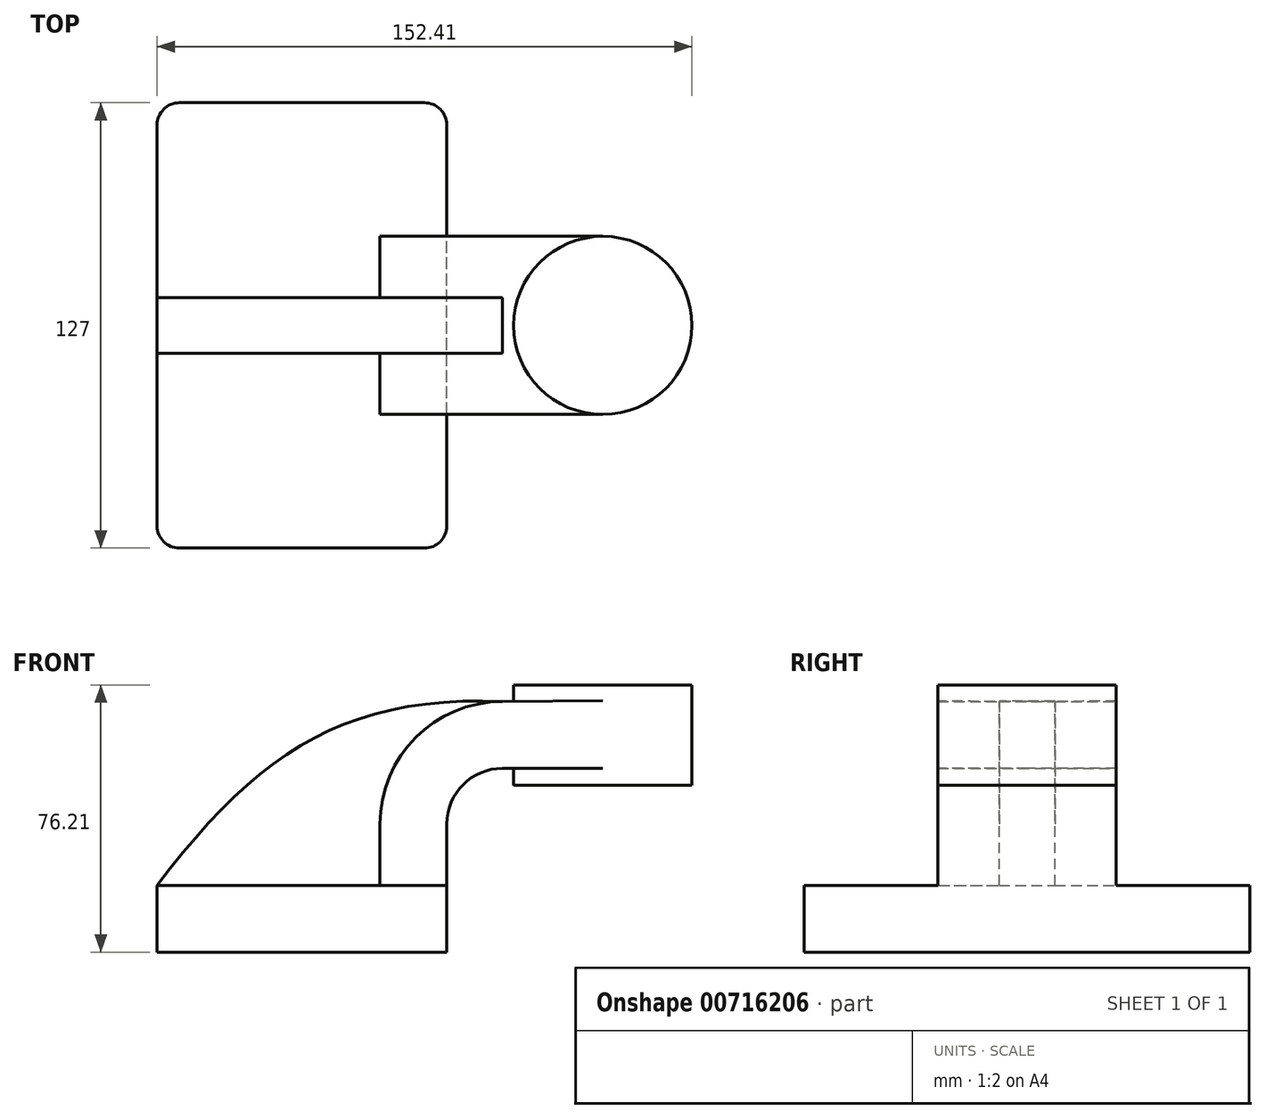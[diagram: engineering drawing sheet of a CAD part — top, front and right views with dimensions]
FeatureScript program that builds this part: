
annotation { "Feature Type Name" : "Feature", "Feature Type Description" : "" }
export const myFeature = defineFeature(function(context is Context, id is Id, definition is map)
    precondition{}
    {
        {
            var Q0;
            Q0=qCreatedBy(makeId("Front.planeOp"),FACE);
            var sketch = newSketch(context, id + "F0", { "sketchPlane" : qUnion([Q0])});
            skLineSegment(sketch, "E0.bottom", {"start": v(-41.28, 9.52) * mm, "end": v(41.28, 9.53) * mm});
            skLineSegment(sketch, "E0.top", {"start": v(-41.27, -9.53) * mm, "end": v(41.28, -9.53) * mm});
            skLineSegment(sketch, "E0.left", {"start": v(-41.28, 9.53) * mm, "end": v(-41.28, -9.53) * mm});
            skLineSegment(sketch, "E0.right", {"start": v(41.27, 9.53) * mm, "end": v(41.28, -9.52) * mm});
            skPoint(sketch, "E0.middle", {"position": v(0, 0) * mm});
            skLineSegment(sketch, "E1.bottom", {"start": v(60.32, 38.1) * mm, "end": v(111.12, 38.1) * mm});
            skLineSegment(sketch, "E1.top", {"start": v(60.32, 66.67) * mm, "end": v(111.12, 66.67) * mm});
            skLineSegment(sketch, "E1.left", {"start": v(60.32, 38.1) * mm, "end": v(60.32, 66.67) * mm});
            skLineSegment(sketch, "E1.right", {"start": v(111.12, 38.1) * mm, "end": v(111.12, 66.67) * mm});
            skPoint(sketch, "E1.middle", {"position": v(85.72, 52.39) * mm});
            skLineSegment(sketch, "E2", {"start": v(41.27, 9.53) * mm, "end": v(41.27, 27) * mm});
            skArc(sketch, "E3", {"start": v(41.27, 27) * mm, "mid": v(45.92, 38.23) * mm, "end": v(57.15, 42.88) * mm});
            skLineSegment(sketch, "E4", {"start": v(57.15, 42.88) * mm, "end": v(113.46, 42.88) * mm});
            skLineSegment(sketch, "E5.2", {"start": v(168.27, 9.53) * mm, "end": v(168.27, 27) * mm});
            skLineSegment(sketch, "E6.0", {"start": v(22.22, 9.53) * mm, "end": v(22.22, 27) * mm});
            skArc(sketch, "E7.0", {"start": v(22.22, 27) * mm, "mid": v(32.45, 51.7) * mm, "end": v(57.15, 61.93) * mm});
            skLineSegment(sketch, "E8", {"start": v(57.15, 61.93) * mm, "end": v(85.72, 62.13) * mm});
            skLineSegment(sketch, "E9", {"start": v(85.72, 38.1) * mm, "end": v(85.72, 66.67) * mm});
            skFitSpline(sketch, "E10", {"points": [v(-41.28, 9.52) * mm, v(57.15, 61.93) * mm], "startDerivative": vector(85.03, 112.26) * mm, "endDerivative": vector(136.02, -5.67) * mm});
            skSolve(sketch);
        }
        {
            var Q0;
            Q0=makeQuery(id+"F0.imprint","IMPRINT",FACE,{"disambiguationData":[TD([[makeQuery(id+"F0.imprint","IMPRINT",EDGE,{"derivedFrom":sQuery(id+"F0.wireOp",EDGE,"E0.top")}),1.0]])]});
            extrude(context, id + "F1", {"entities" : qUnion([Q0]), "endBound" : BoundingType.SYMMETRIC, "depth" : 127 * mm, "offsetDistance" : 25.4 * mm});
        }
        {
            var Q0;
            {var subQ0=sQuery(id+"F0.wireOp",EDGE,"E2");Q0=makeQuery(id+"F0.imprint","IMPRINT",FACE,{"disambiguationData":[TD([[makeQuery(id+"F0.imprint","IMPRINT",EDGE,{"derivedFrom":subQ0}),1.0]])]});}
            var Q1;
            {var subQ0=sQuery(id+"F0.wireOp",EDGE,"E4");var subQ1=sQuery(id+"F0.wireOp",EDGE,"E1.left");var subQ2=makeQuery(id+"F0.imprint","INTERSECT",VERTEX,{"derivedFrom":[subQ1,subQ0]});Q1=makeQuery(id+"F0.imprint","IMPRINT",FACE,{"disambiguationData":[TD([[makeQuery(id+"F0.imprint","IMPRINT",EDGE,{"disambiguationData":[TD([[subQ2,-1.0]])],"derivedFrom":subQ1}),-1.0]])]});}
            extrude(context, id + "F2", {"entities" : qUnion([Q0, Q1]), "operationType" : NewBodyOperationType.ADD, "endBound" : BoundingType.SYMMETRIC, "depth" : 50.8 * mm, "offsetDistance" : 25.4 * mm});
        }
        {
            var Q0;
            {var subQ2=sQuery(id+"F0.wireOp",EDGE,"E6.0");Q0=makeQuery(id+"F0.imprint","IMPRINT",FACE,{"disambiguationData":[TD([[makeQuery(id+"F0.imprint","IMPRINT",EDGE,{"derivedFrom":subQ2}),1.0]])]});}
            extrude(context, id + "F3", {"entities" : qUnion([Q0]), "operationType" : NewBodyOperationType.ADD, "endBound" : BoundingType.SYMMETRIC, "depth" : 15.88 * mm, "offsetDistance" : 25.4 * mm});
        }
        {
            var Q0;
            {var subQ4=sQuery(id+"F0.wireOp",EDGE,"E1.right");var subQ5=sQuery(id+"F0.wireOp",EDGE,"E1.top");var subQ6=makeQuery(id+"F0.imprint","INTERSECT",VERTEX,{"derivedFrom":[subQ5,subQ4]});Q0=makeQuery(id+"F0.imprint","IMPRINT",FACE,{"disambiguationData":[TD([[makeQuery(id+"F0.imprint","IMPRINT",EDGE,{"disambiguationData":[TD([[subQ6,1.0]])],"derivedFrom":subQ5}),-1.0]])]});}
            var Q1;
            {var subQ0=sQuery(id+"F0.wireOp",EDGE,"E1.right");var subQ1=sQuery(id+"F0.wireOp",EDGE,"E1.bottom");var subQ2=makeQuery(id+"F0.imprint","INTERSECT",VERTEX,{"derivedFrom":[subQ1,subQ0]});Q1=makeQuery(id+"F0.imprint","IMPRINT",FACE,{"disambiguationData":[TD([[makeQuery(id+"F0.imprint","IMPRINT",EDGE,{"disambiguationData":[TD([[subQ2,1.0]])],"derivedFrom":subQ1}),1.0]])]});}
            var Q2;
            Q2=sQuery(id+"F0.wireOp",EDGE,"E9");
            revolve(context, id + "F4", {"operationType" : NewBodyOperationType.ADD, "surfaceOperationType" : NewSurfaceOperationType.NEW, "entities" : qUnion([Q0, Q1]), "axis" : qUnion([Q2]), "revolveType" : RevolveType.FULL});
        }
        {
            var Q0;
            Q0=makeQuery(id+"F1.opExtrude","CAP_EDGE",EDGE,{"disambiguationData":[OSD([sQuery(id+"F0.wireOp",EDGE,"E0.left")])],"isStart":false});
            var Q1;
            Q1=makeQuery(id+"F1.opExtrude","CAP_EDGE",EDGE,{"disambiguationData":[OSD([sQuery(id+"F0.wireOp",EDGE,"E0.right")])],"isStart":false});
            var Q2;
            Q2=makeQuery(id+"F1.opExtrude","CAP_EDGE",EDGE,{"disambiguationData":[OSD([sQuery(id+"F0.wireOp",EDGE,"E0.right")])],"isStart":true});
            var Q3;
            Q3=makeQuery(id+"F1.opExtrude","CAP_EDGE",EDGE,{"disambiguationData":[OSD([sQuery(id+"F0.wireOp",EDGE,"E0.left")])],"isStart":true});
            fillet(context, id + "F5", {"entities" : qUnion([Q0, Q1, Q2, Q3]), "radius" : 6.35 * mm, "tangentPropagation" : true, "allowEdgeOverflow" : false});
        }
    });
